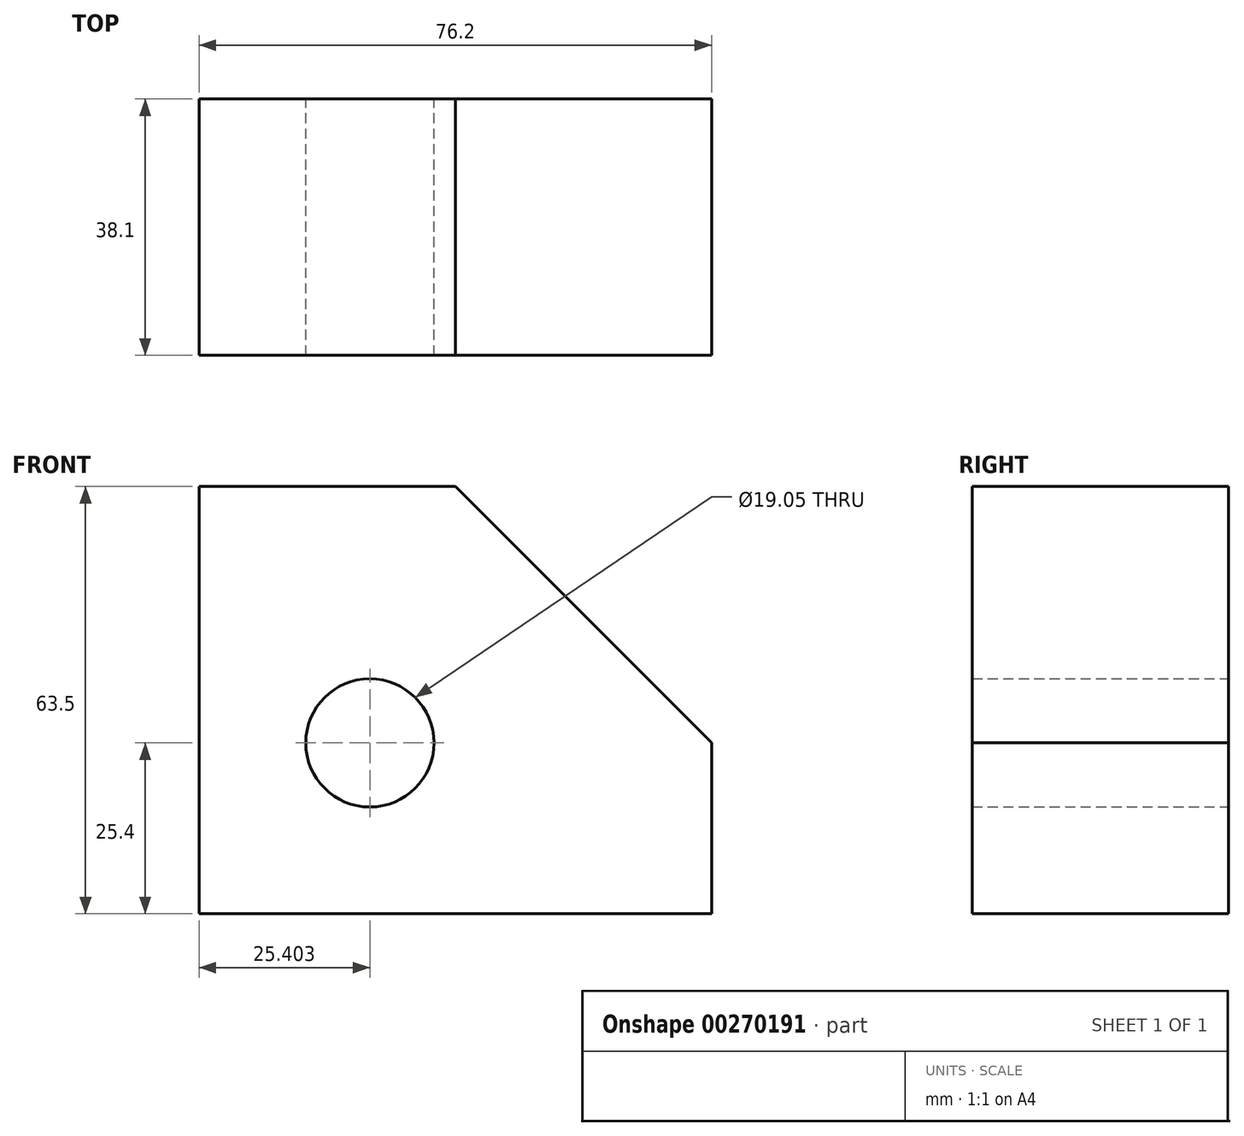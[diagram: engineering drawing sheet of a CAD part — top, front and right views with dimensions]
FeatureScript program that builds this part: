
annotation { "Feature Type Name" : "Feature", "Feature Type Description" : "" }
export const myFeature = defineFeature(function(context is Context, id is Id, definition is map)
    precondition{}
    {
        {
            var Q0;
            Q0=qCreatedBy(makeId("Front.planeOp"),FACE);
            var sketch = newSketch(context, id + "F0", { "sketchPlane" : qUnion([Q0])});
            skLineSegment(sketch, "E0", {"start": v(-42.24, 63.5) * mm, "end": v(-42.24, 0) * mm});
            skLineSegment(sketch, "E1", {"start": v(-42.24, 0) * mm, "end": v(33.96, 0) * mm});
            skLineSegment(sketch, "E2", {"start": v(33.96, 0) * mm, "end": v(33.96, 25.4) * mm});
            skLineSegment(sketch, "E3", {"start": v(-42.24, 63.5) * mm, "end": v(-4.14, 63.5) * mm});
            skLineSegment(sketch, "E4", {"start": v(-4.14, 63.5) * mm, "end": v(33.96, 25.4) * mm});
            skCircle(sketch, "E5", {"center": v(-16.84, 25.4) * mm, "radius": 9.53 * mm});
            skSolve(sketch);
        }
        {
            var Q0;
            Q0=qSketchRegion(id+"F0",true);
            extrude(context, id + "F1", {"entities" : qUnion([Q0]), "depth" : 38.1 * mm, "symmetric" : true});
        }
    });
